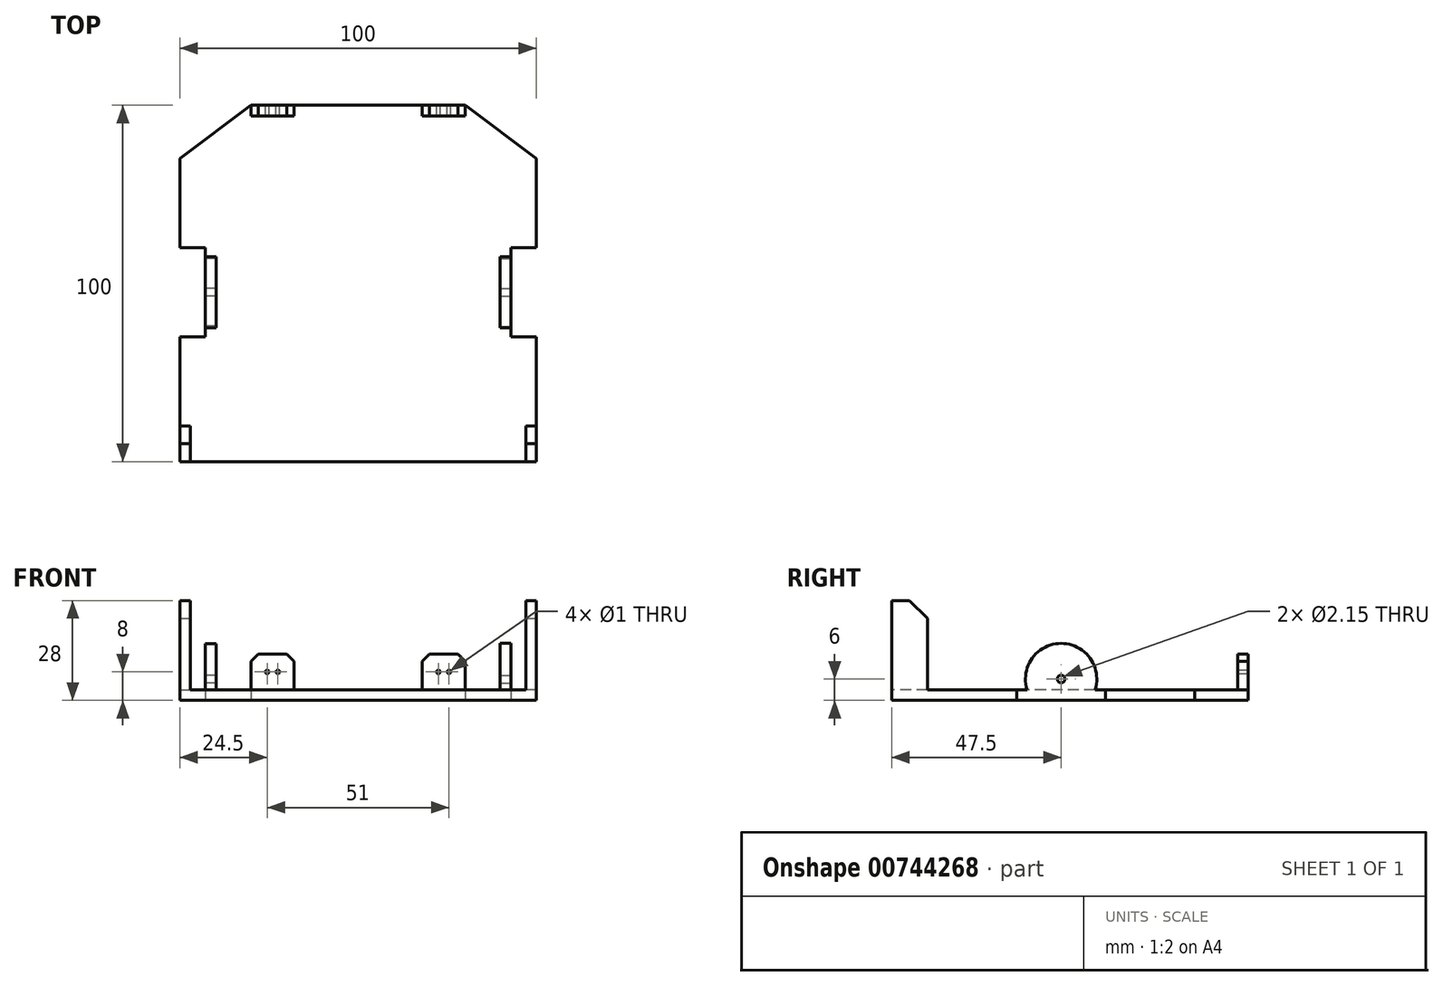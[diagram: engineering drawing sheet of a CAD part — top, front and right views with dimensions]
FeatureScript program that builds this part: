
annotation { "Feature Type Name" : "Feature", "Feature Type Description" : "" }
export const myFeature = defineFeature(function(context is Context, id is Id, definition is map)
    precondition{}
    {
        {
            var Q0;
            Q0=qCreatedBy(makeId("Top.planeOp"),FACE);
            var sketch = newSketch(context, id + "F0", { "sketchPlane" : qUnion([Q0])});
            skLineSegment(sketch, "E0", {"start": v(-30, 56.12) * mm, "end": v(30, 56.12) * mm});
            skLineSegment(sketch, "E1", {"start": v(30, 56.12) * mm, "end": v(50, 41.12) * mm});
            skLineSegment(sketch, "E2", {"start": v(-30, 56.12) * mm, "end": v(-50, 41.12) * mm});
            skLineSegment(sketch, "E3", {"start": v(-50, 41.12) * mm, "end": v(-50, 16.12) * mm});
            skLineSegment(sketch, "E4", {"start": v(-50, 16.12) * mm, "end": v(-42.8, 16.12) * mm});
            skLineSegment(sketch, "E5", {"start": v(-42.8, 16.12) * mm, "end": v(-42.8, -8.88) * mm});
            skLineSegment(sketch, "E6", {"start": v(-42.8, -8.88) * mm, "end": v(-50, -8.88) * mm});
            skLineSegment(sketch, "E7", {"start": v(-50, -8.88) * mm, "end": v(-50, -68.88) * mm});
            skLineSegment(sketch, "E8", {"start": v(-50, -68.88) * mm, "end": v(-39.78, -68.88) * mm});
            skLineSegment(sketch, "E9", {"start": v(-39.78, -68.88) * mm, "end": v(-39.78, -103.88) * mm});
            skLineSegment(sketch, "E10", {"start": v(-39.78, -103.88) * mm, "end": v(-50, -103.88) * mm});
            skLineSegment(sketch, "E11", {"start": v(-50, -103.88) * mm, "end": v(-50, -113.88) * mm});
            skLineSegment(sketch, "E12", {"start": v(-50, -113.88) * mm, "end": v(-40, -123.88) * mm});
            skLineSegment(sketch, "E13", {"start": v(-40, -123.88) * mm, "end": v(40, -123.88) * mm});
            skLineSegment(sketch, "E14.MirrorCS", {"start": v(50, 41.12) * mm, "end": v(50, 16.12) * mm});
            skLineSegment(sketch, "E15.MirrorCS", {"start": v(50, 16.12) * mm, "end": v(42.8, 16.12) * mm});
            skLineSegment(sketch, "E16.MirrorCS", {"start": v(42.8, 16.12) * mm, "end": v(42.8, -8.88) * mm});
            skLineSegment(sketch, "E17.MirrorCS", {"start": v(42.8, -8.88) * mm, "end": v(50, -8.88) * mm});
            skLineSegment(sketch, "E18.MirrorCS", {"start": v(50, -8.88) * mm, "end": v(50, -68.88) * mm});
            skLineSegment(sketch, "E19.MirrorCS", {"start": v(50, -68.88) * mm, "end": v(39.78, -68.88) * mm});
            skLineSegment(sketch, "E20.MirrorCS", {"start": v(39.78, -68.88) * mm, "end": v(39.78, -103.88) * mm});
            skLineSegment(sketch, "E21.MirrorCS", {"start": v(39.78, -103.88) * mm, "end": v(50, -103.88) * mm});
            skLineSegment(sketch, "E22.MirrorCS", {"start": v(50, -103.88) * mm, "end": v(50, -113.88) * mm});
            skLineSegment(sketch, "E23.MirrorCS", {"start": v(50, -113.88) * mm, "end": v(40, -123.88) * mm});
            skLineSegment(sketch, "E24", {"start": v(-50, -43.88) * mm, "end": v(50, -43.88) * mm});
            skSolve(sketch);
        }
        {
            var Q0;
            Q0=makeQuery(id+"F0.imprint","IMPRINT",FACE,{"disambiguationData":[TD([[makeQuery(id+"F0.imprint","IMPRINT",EDGE,{"derivedFrom":sQuery(id+"F0.wireOp",EDGE,"E0")}),-1.0]])]});
            extrude(context, id + "F1", {"entities" : qUnion([Q0]), "depth" : 3 * mm, "offsetDistance" : 25 * mm});
        }
        {
            var Q0;
            Q0=makeQuery(id+"F1.opExtrude","SWEPT_FACE",FACE,{"disambiguationData":[OSD([sQuery(id+"F0.wireOp",EDGE,"E16.MirrorCS")])]});
            var sketch = newSketch(context, id + "F2", { "sketchPlane" : qUnion([Q0])});
            skArc(sketch, "E25", {"start": v(13.16, 3) * mm, "mid": v(3.62, 16) * mm, "end": v(-5.92, 3) * mm});
            skCircle(sketch, "E26", {"center": v(3.62, 6) * mm, "radius": 1.07 * mm});
            skSolve(sketch);
        }
        {
            var Q0;
            {var subQ0=sQuery(id+"F2.wireOp",EDGE,"E25");Q0=makeQuery(id+"F2.imprint","IMPRINT",FACE,{"disambiguationData":[TD([[makeQuery(id+"F2.imprint","IMPRINT",EDGE,{"derivedFrom":subQ0}),1.0]])]});}
            extrude(context, id + "F3", {"entities" : qUnion([Q0]), "operationType" : NewBodyOperationType.ADD, "oppositeDirection" : true, "depth" : 3 * mm, "offsetDistance" : 25 * mm});
        }
        {
            var Q0;
            Q0=makeQuery(id+"F1.opExtrude","SWEPT_FACE",FACE,{"disambiguationData":[OSD([sQuery(id+"F0.wireOp",EDGE,"E5")])]});
            var sketch = newSketch(context, id + "F4", { "sketchPlane" : qUnion([Q0])});
            skArc(sketch, "E27", {"start": v(5.86, 3) * mm, "mid": v(-3.62, 15.94) * mm, "end": v(-13.1, 3) * mm});
            skCircle(sketch, "E28", {"center": v(-3.62, 6) * mm, "radius": 1.07 * mm});
            skSolve(sketch);
        }
        {
            var Q0;
            {var subQ0=sQuery(id+"F4.wireOp",EDGE,"E27");Q0=makeQuery(id+"F4.imprint","IMPRINT",FACE,{"disambiguationData":[TD([[makeQuery(id+"F4.imprint","IMPRINT",EDGE,{"derivedFrom":subQ0}),1.0]])]});}
            extrude(context, id + "F5", {"entities" : qUnion([Q0]), "operationType" : NewBodyOperationType.ADD, "oppositeDirection" : true, "depth" : 3 * mm, "offsetDistance" : 25 * mm});
        }
        {
            var Q0;
            Q0=makeQuery(id+"F1.opExtrude","CAP_FACE",FACE,{"disambiguationData":[OSD([sQuery(id+"F0.wireOp",EDGE,"E0"),sQuery(id+"F0.wireOp",EDGE,"E1"),sQuery(id+"F0.wireOp",EDGE,"E2"),sQuery(id+"F0.wireOp",EDGE,"E3"),sQuery(id+"F0.wireOp",EDGE,"E4"),sQuery(id+"F0.wireOp",EDGE,"E5"),sQuery(id+"F0.wireOp",EDGE,"E6"),sQuery(id+"F0.wireOp",EDGE,"E7"),sQuery(id+"F0.wireOp",EDGE,"E8"),sQuery(id+"F0.wireOp",EDGE,"E9"),sQuery(id+"F0.wireOp",EDGE,"E10"),sQuery(id+"F0.wireOp",EDGE,"E11"),sQuery(id+"F0.wireOp",EDGE,"E12"),sQuery(id+"F0.wireOp",EDGE,"E13"),sQuery(id+"F0.wireOp",EDGE,"E14.MirrorCS"),sQuery(id+"F0.wireOp",EDGE,"E15.MirrorCS"),sQuery(id+"F0.wireOp",EDGE,"E16.MirrorCS"),sQuery(id+"F0.wireOp",EDGE,"E17.MirrorCS"),sQuery(id+"F0.wireOp",EDGE,"E18.MirrorCS"),sQuery(id+"F0.wireOp",EDGE,"E19.MirrorCS"),sQuery(id+"F0.wireOp",EDGE,"E20.MirrorCS"),sQuery(id+"F0.wireOp",EDGE,"E21.MirrorCS"),sQuery(id+"F0.wireOp",EDGE,"E22.MirrorCS"),sQuery(id+"F0.wireOp",EDGE,"E23.MirrorCS")])],"isStart":false});
            var sketch = newSketch(context, id + "F6", { "sketchPlane" : qUnion([Q0])});
            skLineSegment(sketch, "E29.bottom", {"start": v(-30, 56.12) * mm, "end": v(-18, 56.12) * mm});
            skLineSegment(sketch, "E29.top", {"start": v(-30, 53.12) * mm, "end": v(-18, 53.12) * mm});
            skLineSegment(sketch, "E29.left", {"start": v(-30, 56.12) * mm, "end": v(-30, 53.12) * mm});
            skLineSegment(sketch, "E29.right", {"start": v(-18, 56.12) * mm, "end": v(-18, 53.12) * mm});
            skLineSegment(sketch, "E30.MirrorCS", {"start": v(30, 53.12) * mm, "end": v(18, 53.12) * mm});
            skLineSegment(sketch, "E31.MirrorCS", {"start": v(30, 56.12) * mm, "end": v(18, 56.12) * mm});
            skLineSegment(sketch, "E32.MirrorCS", {"start": v(18, 56.12) * mm, "end": v(18, 53.12) * mm});
            skLineSegment(sketch, "E33.MirrorCS", {"start": v(30, 56.12) * mm, "end": v(30, 53.12) * mm});
            skSolve(sketch);
        }
        {
            var Q0;
            Q0 = qSketchRegion(id + "F6", true);
            extrude(context, id + "F7", {"entities" : qUnion([Q0]), "operationType" : NewBodyOperationType.ADD, "depth" : 10 * mm, "offsetDistance" : 25 * mm});
        }
        {
            var Q0;
            Q0=makeQuery(id+"F7.boolean.opBoolean","MERGE",FACE,{"derivedFrom":[makeQuery(id+"F1.opExtrude","SWEPT_FACE",FACE,{"disambiguationData":[OSD([sQuery(id+"F0.wireOp",EDGE,"E0")])]}),makeQuery(id+"F7.opExtrude","SWEPT_FACE",FACE,{"disambiguationData":[OSD([sQuery(id+"F6.wireOp",EDGE,"E29.bottom")])]}),makeQuery(id+"F7.opExtrude","SWEPT_FACE",FACE,{"disambiguationData":[OSD([sQuery(id+"F6.wireOp",EDGE,"E31.MirrorCS")])]})]});
            var sketch = newSketch(context, id + "F8", { "sketchPlane" : qUnion([Q0])});
            skCircle(sketch, "E34", {"center": v(-25.5, 8) * mm, "radius": 0.5 * mm});
            skPoint(sketch, "E34.centerSnap0", {"position": v(-30, 8) * mm});
            skCircle(sketch, "E35", {"center": v(-22.5, 8) * mm, "radius": 0.5 * mm});
            skCircle(sketch, "E36.MirrorC", {"center": v(25.5, 8) * mm, "radius": 0.5 * mm});
            skCircle(sketch, "E37.MirrorC", {"center": v(22.5, 8) * mm, "radius": 0.5 * mm});
            skSolve(sketch);
        }
        {
            var Q0;
            Q0 = qSketchRegion(id + "F8", true);
            extrude(context, id + "F9", {"entities" : qUnion([Q0]), "operationType" : NewBodyOperationType.REMOVE, "endBound" : BoundingType.UP_TO_NEXT, "oppositeDirection" : true, "depth" : 25 * mm, "offsetDistance" : 25 * mm});
        }
        {
            var Q0;
            Q0=makeQuery(id+"F7.opExtrude","CAP_EDGE",EDGE,{"disambiguationData":[OSD([sQuery(id+"F6.wireOp",EDGE,"E32.MirrorCS")])],"isStart":false});
            var Q1;
            Q1=makeQuery(id+"F7.opExtrude","CAP_EDGE",EDGE,{"disambiguationData":[OSD([sQuery(id+"F6.wireOp",EDGE,"E33.MirrorCS")])],"isStart":false});
            var Q2;
            Q2=makeQuery(id+"F7.opExtrude","CAP_EDGE",EDGE,{"disambiguationData":[OSD([sQuery(id+"F6.wireOp",EDGE,"E29.right")])],"isStart":false});
            var Q3;
            Q3=makeQuery(id+"F7.opExtrude","CAP_EDGE",EDGE,{"disambiguationData":[OSD([sQuery(id+"F6.wireOp",EDGE,"E29.left")])],"isStart":false});
            var Q4;
            Q4=makeQuery(id+"F7.opExtrude","CAP_EDGE",EDGE,{"disambiguationData":[OSD([sQuery(id+"F6.wireOp",EDGE,"1paxiMkq-f3b9-XHE5-rruL-BWlCMyREupKs.left")])],"isStart":false});
            var Q5;
            Q5=makeQuery(id+"F7.opExtrude","CAP_EDGE",EDGE,{"disambiguationData":[OSD([sQuery(id+"F6.wireOp",EDGE,"1paxiMkq-f3b9-XHE5-rruL-BWlCMyREupKs.right")])],"isStart":false});
            var Q6;
            Q6=makeQuery(id+"F7.opExtrude","CAP_EDGE",EDGE,{"disambiguationData":[OSD([sQuery(id+"F6.wireOp",EDGE,"VCSGi1VB-V47J-YXb4-d8Nq-2kGsya5thd09.right")])],"isStart":false});
            var Q7;
            Q7=makeQuery(id+"F7.opExtrude","CAP_EDGE",EDGE,{"disambiguationData":[OSD([sQuery(id+"F6.wireOp",EDGE,"VCSGi1VB-V47J-YXb4-d8Nq-2kGsya5thd09.left")])],"isStart":false});
            chamfer(context, id + "F10", {"entities" : qUnion([Q0, Q1, Q2, Q3, Q4, Q5, Q6, Q7]), "width" : 2 * mm, "tangentPropagation" : true});
        }
        {
            var Q0;
            Q0=makeQuery(id+"F1.opExtrude","CAP_FACE",FACE,{"disambiguationData":[OSD([sQuery(id+"F0.wireOp",EDGE,"E0"),sQuery(id+"F0.wireOp",EDGE,"E1"),sQuery(id+"F0.wireOp",EDGE,"E2"),sQuery(id+"F0.wireOp",EDGE,"E3"),sQuery(id+"F0.wireOp",EDGE,"E4"),sQuery(id+"F0.wireOp",EDGE,"E5"),sQuery(id+"F0.wireOp",EDGE,"E6"),sQuery(id+"F0.wireOp",EDGE,"E7"),sQuery(id+"F0.wireOp",EDGE,"E8"),sQuery(id+"F0.wireOp",EDGE,"E9"),sQuery(id+"F0.wireOp",EDGE,"E10"),sQuery(id+"F0.wireOp",EDGE,"E11"),sQuery(id+"F0.wireOp",EDGE,"E12"),sQuery(id+"F0.wireOp",EDGE,"E13"),sQuery(id+"F0.wireOp",EDGE,"E14.MirrorCS"),sQuery(id+"F0.wireOp",EDGE,"E15.MirrorCS"),sQuery(id+"F0.wireOp",EDGE,"E16.MirrorCS"),sQuery(id+"F0.wireOp",EDGE,"E17.MirrorCS"),sQuery(id+"F0.wireOp",EDGE,"E18.MirrorCS"),sQuery(id+"F0.wireOp",EDGE,"E19.MirrorCS"),sQuery(id+"F0.wireOp",EDGE,"E20.MirrorCS"),sQuery(id+"F0.wireOp",EDGE,"E21.MirrorCS"),sQuery(id+"F0.wireOp",EDGE,"E22.MirrorCS"),sQuery(id+"F0.wireOp",EDGE,"E23.MirrorCS")])],"isStart":false});
            var sketch = newSketch(context, id + "F11", { "sketchPlane" : qUnion([Q0])});
            skLineSegment(sketch, "E38.bottom", {"start": v(50, -33.88) * mm, "end": v(47, -33.88) * mm});
            skLineSegment(sketch, "E38.top", {"start": v(50, -43.88) * mm, "end": v(47, -43.88) * mm});
            skLineSegment(sketch, "E38.left", {"start": v(50, -33.88) * mm, "end": v(50, -43.88) * mm});
            skLineSegment(sketch, "E38.right", {"start": v(47, -33.88) * mm, "end": v(47, -43.88) * mm});
            skLineSegment(sketch, "E39.MirrorCS", {"start": v(-47, -33.88) * mm, "end": v(-47, -43.88) * mm});
            skLineSegment(sketch, "E40.MirrorCS", {"start": v(-50, -33.88) * mm, "end": v(-47, -33.88) * mm});
            skLineSegment(sketch, "E41.MirrorCS", {"start": v(-50, -43.88) * mm, "end": v(-47, -43.88) * mm});
            skLineSegment(sketch, "E42.MirrorCS", {"start": v(-50, -33.88) * mm, "end": v(-50, -43.88) * mm});
            skSolve(sketch);
        }
        {
            var Q0;
            Q0 = qSketchRegion(id + "F11", true);
            extrude(context, id + "F12", {"entities" : qUnion([Q0]), "operationType" : NewBodyOperationType.ADD, "depth" : 25 * mm, "offsetDistance" : 25 * mm});
        }
        {
            var Q0;
            Q0=makeQuery(id+"F12.opExtrude","CAP_EDGE",EDGE,{"disambiguationData":[OSD([sQuery(id+"F11.wireOp",EDGE,"E40.MirrorCS")])],"isStart":false});
            var Q1;
            Q1=makeQuery(id+"F12.opExtrude","CAP_EDGE",EDGE,{"disambiguationData":[OSD([sQuery(id+"F11.wireOp",EDGE,"E38.bottom")])],"isStart":false});
            chamfer(context, id + "F13", {"entities" : qUnion([Q0, Q1]), "width" : 5 * mm, "tangentPropagation" : true});
        }
    });
